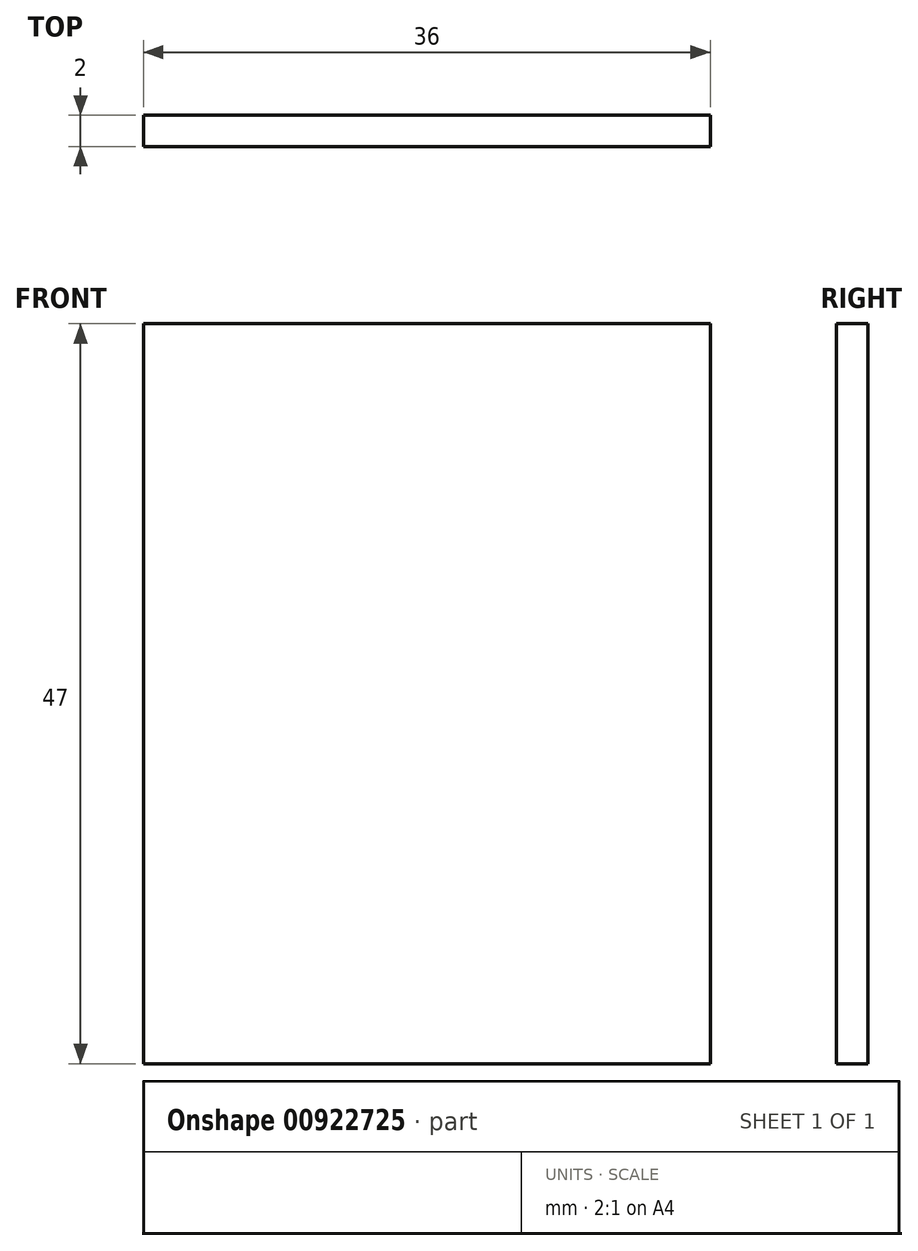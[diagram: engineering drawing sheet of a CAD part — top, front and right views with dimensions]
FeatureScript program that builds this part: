
annotation { "Feature Type Name" : "Feature", "Feature Type Description" : "" }
export const myFeature = defineFeature(function(context is Context, id is Id, definition is map)
    precondition{}
    {
        {
            var Q0;
            Q0=qCreatedBy(makeId("Front.planeOp"),FACE);
            var sketch = newSketch(context, id + "F0", { "sketchPlane" : qUnion([Q0])});
            skLineSegment(sketch, "E0.bottom", {"start": v(18, -23.5) * mm, "end": v(-18, -23.5) * mm});
            skLineSegment(sketch, "E0.top", {"start": v(18, 23.5) * mm, "end": v(-18, 23.5) * mm});
            skLineSegment(sketch, "E0.left", {"start": v(18, -23.5) * mm, "end": v(18, 23.5) * mm});
            skLineSegment(sketch, "E0.right", {"start": v(-18, -23.5) * mm, "end": v(-18, 23.5) * mm});
            skPoint(sketch, "E0.middle", {"position": v(0, 0) * mm});
            skSolve(sketch);
        }
        {
            var Q0;
            Q0 = qSketchRegion(id + "F0", true);
            extrude(context, id + "F1", {"entities" : qUnion([Q0]), "endBound" : BoundingType.SYMMETRIC, "depth" : 2 * mm, "offsetDistance" : 25 * mm});
        }
    });
